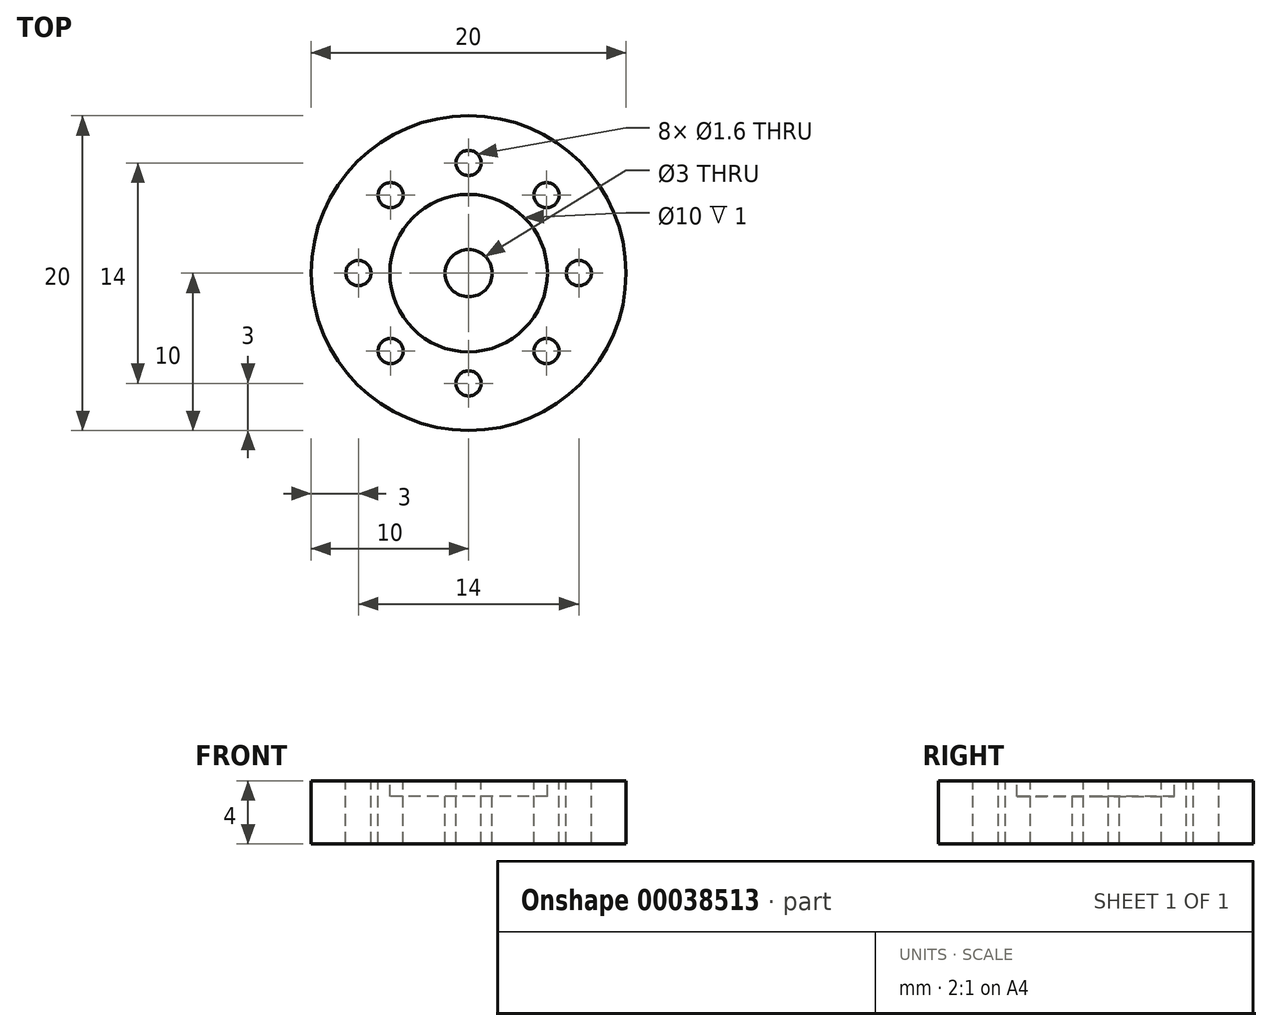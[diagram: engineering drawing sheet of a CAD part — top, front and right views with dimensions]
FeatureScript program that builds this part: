
annotation { "Feature Type Name" : "Feature", "Feature Type Description" : "" }
export const myFeature = defineFeature(function(context is Context, id is Id, definition is map)
    precondition{}
    {
        {
            var Q0;
            Q0=qCreatedBy(makeId("Top.planeOp"),FACE);
            var sketch = newSketch(context, id + "F0", { "sketchPlane" : qUnion([Q0])});
            skCircle(sketch, "E0", {"center": v(0, 0) * mm, "radius": 10 * mm});
            skCircle(sketch, "E1", {"center": v(0, 0) * mm, "radius": 5 * mm});
            skCircle(sketch, "E2", {"center": v(0, 0) * mm, "radius": 1.5 * mm});
            skCircle(sketch, "E3", {"center": v(0, 0) * mm, "radius": 7 * mm, "construction": true});
            skLineSegment(sketch, "E4", {"start": v(0, 0) * mm, "end": v(0, 7) * mm, "construction": true});
            skLineSegment(sketch, "E5", {"start": v(0, 0) * mm, "end": v(-7, 0) * mm, "construction": true});
            skPoint(sketch, "E6", {"position": v(-4.95, 4.95) * mm});
            skCircle(sketch, "E7", {"center": v(-4.95, 4.95) * mm, "radius": 0.8 * mm});
            skCircle(sketch, "E8", {"center": v(0, 7) * mm, "radius": 0.8 * mm});
            skCircle(sketch, "E9", {"center": v(-7, 0) * mm, "radius": 0.8 * mm});
            skCircle(sketch, "E10.MirrorC", {"center": v(4.95, 4.95) * mm, "radius": 0.8 * mm});
            skCircle(sketch, "E11.MirrorC", {"center": v(7, 0) * mm, "radius": 0.8 * mm});
            skCircle(sketch, "E12.MirrorC", {"center": v(-4.95, -4.95) * mm, "radius": 0.8 * mm});
            skCircle(sketch, "E13.MirrorC", {"center": v(0, -7) * mm, "radius": 0.8 * mm});
            skCircle(sketch, "E14.MirrorC", {"center": v(4.95, -4.95) * mm, "radius": 0.8 * mm});
            skSolve(sketch);
        }
        {
            var Q0;
            Q0=makeQuery(id+"F0.imprint","IMPRINT",FACE,{"disambiguationData":[TD([[makeQuery(id+"F0.imprint","IMPRINT",EDGE,{"derivedFrom":sQuery(id+"F0.wireOp",EDGE,"E0")}),1.0]])]});
            var Q1;
            Q1=makeQuery(id+"F0.imprint","IMPRINT",FACE,{"disambiguationData":[TD([[makeQuery(id+"F0.imprint","IMPRINT",EDGE,{"derivedFrom":sQuery(id+"F0.wireOp",EDGE,"E1")}),1.0]])]});
            extrude(context, id + "F1", {"entities" : qUnion([Q0, Q1]), "oppositeDirection" : true, "depth" : 4 * mm, "offsetDistance" : 25 * mm});
        }
        {
            var Q0;
            Q0=makeQuery(id+"F0.imprint","IMPRINT",FACE,{"disambiguationData":[TD([[makeQuery(id+"F0.imprint","IMPRINT",EDGE,{"derivedFrom":sQuery(id+"F0.wireOp",EDGE,"E1")}),1.0]])]});
            extrude(context, id + "F2", {"entities" : qUnion([Q0]), "operationType" : NewBodyOperationType.REMOVE, "oppositeDirection" : true, "depth" : 1 * mm, "offsetDistance" : 25 * mm});
        }
    });
